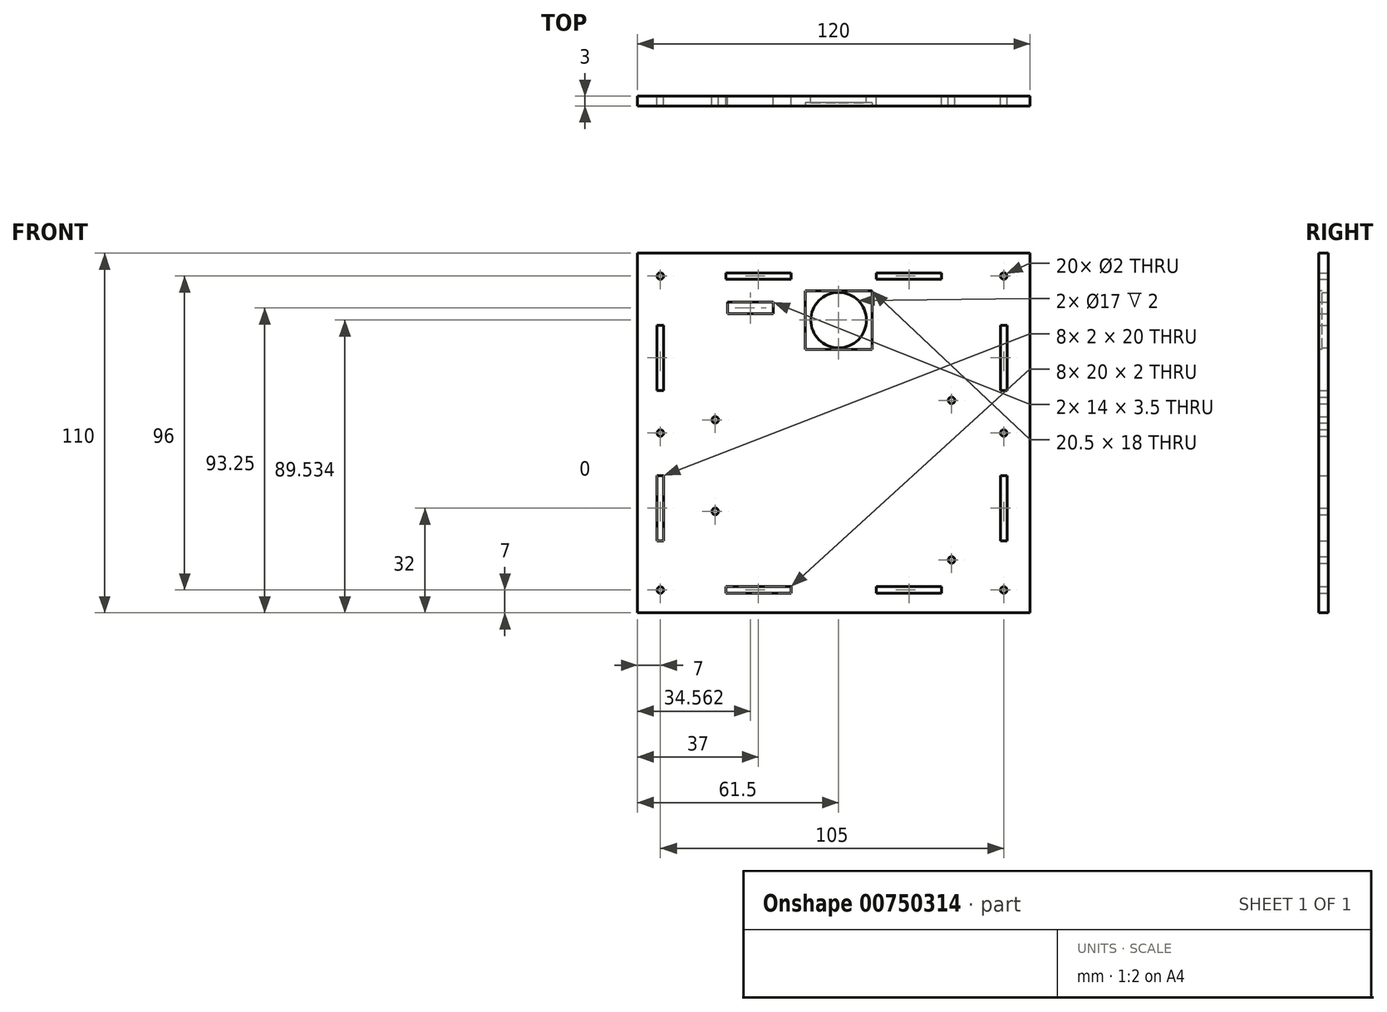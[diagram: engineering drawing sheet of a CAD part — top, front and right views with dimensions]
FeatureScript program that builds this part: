
annotation { "Feature Type Name" : "Feature", "Feature Type Description" : "" }
export const myFeature = defineFeature(function(context is Context, id is Id, definition is map)
    precondition{}
    {
        {
            var Q0;
            Q0=qCreatedBy(makeId("Front.planeOp"),FACE);
            var sketch = newSketch(context, id + "F0", { "sketchPlane" : qUnion([Q0])});
            skLineSegment(sketch, "E0.bottom", {"start": v(60, -55) * mm, "end": v(-60, -55) * mm});
            skLineSegment(sketch, "E0.top", {"start": v(60, 55) * mm, "end": v(-60, 55) * mm});
            skLineSegment(sketch, "E0.left", {"start": v(60, -55) * mm, "end": v(60, 55) * mm});
            skLineSegment(sketch, "E0.right", {"start": v(-60, -55) * mm, "end": v(-60, 55) * mm});
            skPoint(sketch, "E0.middle", {"position": v(0, 0) * mm});
            skCircle(sketch, "E1", {"center": v(1.5, 34.53) * mm, "radius": 8.5 * mm});
            skLineSegment(sketch, "E2.bottom", {"start": v(-18.44, 36.5) * mm, "end": v(-32.44, 36.5) * mm});
            skLineSegment(sketch, "E2.top", {"start": v(-18.44, 40) * mm, "end": v(-32.44, 40) * mm});
            skLineSegment(sketch, "E2.left", {"start": v(-18.44, 36.5) * mm, "end": v(-18.44, 40) * mm});
            skLineSegment(sketch, "E2.right", {"start": v(-32.44, 36.5) * mm, "end": v(-32.44, 40) * mm});
            skPoint(sketch, "E2.middle", {"position": v(-25.44, 38.25) * mm});
            skCircle(sketch, "E3", {"center": v(36.03, 10) * mm, "radius": 1 * mm});
            skCircle(sketch, "E4", {"center": v(36.03, -38.8) * mm, "radius": 1 * mm});
            skCircle(sketch, "E5", {"center": v(-36.22, 4.04) * mm, "radius": 1 * mm});
            skCircle(sketch, "E6", {"center": v(-36.22, -23.96) * mm, "radius": 1 * mm});
            skCircle(sketch, "E7", {"center": v(-53, 48) * mm, "radius": 1 * mm});
            skCircle(sketch, "E8", {"center": v(-53, -48) * mm, "radius": 1 * mm});
            skCircle(sketch, "E9", {"center": v(52, -48) * mm, "radius": 1 * mm});
            skCircle(sketch, "E10", {"center": v(52, 48) * mm, "radius": 1 * mm});
            skCircle(sketch, "E11", {"center": v(-53, 0) * mm, "radius": 1 * mm});
            skCircle(sketch, "E12", {"center": v(52, 0) * mm, "radius": 1 * mm});
            skLineSegment(sketch, "E13.bottom", {"start": v(-52, 33) * mm, "end": v(-54, 33) * mm});
            skLineSegment(sketch, "E13.top", {"start": v(-52, 13) * mm, "end": v(-54, 13) * mm});
            skLineSegment(sketch, "E13.left", {"start": v(-52, 33) * mm, "end": v(-52, 13) * mm});
            skLineSegment(sketch, "E13.right", {"start": v(-54, 33) * mm, "end": v(-54, 13) * mm});
            skPoint(sketch, "E13.middle", {"position": v(-53, 23) * mm});
            skLineSegment(sketch, "E14.bottom", {"start": v(-52, -33) * mm, "end": v(-54, -33) * mm});
            skLineSegment(sketch, "E14.top", {"start": v(-52, -13) * mm, "end": v(-54, -13) * mm});
            skLineSegment(sketch, "E14.left", {"start": v(-52, -33) * mm, "end": v(-52, -13) * mm});
            skLineSegment(sketch, "E14.right", {"start": v(-54, -33) * mm, "end": v(-54, -13) * mm});
            skPoint(sketch, "E14.middle", {"position": v(-53, -23) * mm});
            skPoint(sketch, "E14.cornerSnap0", {"position": v(-52, 23) * mm});
            skLineSegment(sketch, "E15.bottom", {"start": v(53, 13) * mm, "end": v(51, 13) * mm});
            skLineSegment(sketch, "E15.top", {"start": v(53, 33) * mm, "end": v(51, 33) * mm});
            skLineSegment(sketch, "E15.left", {"start": v(53, 13) * mm, "end": v(53, 33) * mm});
            skLineSegment(sketch, "E15.right", {"start": v(51, 13) * mm, "end": v(51, 33) * mm});
            skPoint(sketch, "E15.middle", {"position": v(52, 23) * mm});
            skLineSegment(sketch, "E16.bottom", {"start": v(53, -33) * mm, "end": v(51, -33) * mm});
            skLineSegment(sketch, "E16.top", {"start": v(53, -13) * mm, "end": v(51, -13) * mm});
            skLineSegment(sketch, "E16.left", {"start": v(53, -33) * mm, "end": v(53, -13) * mm});
            skLineSegment(sketch, "E16.right", {"start": v(51, -33) * mm, "end": v(51, -13) * mm});
            skPoint(sketch, "E16.middle", {"position": v(52, -23) * mm});
            skLineSegment(sketch, "E17.bottom", {"start": v(-13, -49) * mm, "end": v(-33, -49) * mm});
            skLineSegment(sketch, "E17.top", {"start": v(-13, -47) * mm, "end": v(-33, -47) * mm});
            skLineSegment(sketch, "E17.left", {"start": v(-13, -49) * mm, "end": v(-13, -47) * mm});
            skLineSegment(sketch, "E17.right", {"start": v(-33, -49) * mm, "end": v(-33, -47) * mm});
            skPoint(sketch, "E17.middle", {"position": v(-23, -48) * mm});
            skLineSegment(sketch, "E18.bottom", {"start": v(33, -49) * mm, "end": v(13, -49) * mm});
            skLineSegment(sketch, "E18.top", {"start": v(33, -47) * mm, "end": v(13, -47) * mm});
            skLineSegment(sketch, "E18.left", {"start": v(33, -49) * mm, "end": v(33, -47) * mm});
            skLineSegment(sketch, "E18.right", {"start": v(13, -49) * mm, "end": v(13, -47) * mm});
            skPoint(sketch, "E18.middle", {"position": v(23, -48) * mm});
            skLineSegment(sketch, "E19.bottom", {"start": v(-13, 47) * mm, "end": v(-33, 47) * mm});
            skLineSegment(sketch, "E19.top", {"start": v(-13, 49) * mm, "end": v(-33, 49) * mm});
            skLineSegment(sketch, "E19.left", {"start": v(-13, 47) * mm, "end": v(-13, 49) * mm});
            skLineSegment(sketch, "E19.right", {"start": v(-33, 47) * mm, "end": v(-33, 49) * mm});
            skPoint(sketch, "E19.middle", {"position": v(-23, 48) * mm});
            skLineSegment(sketch, "E20.bottom", {"start": v(33, 47) * mm, "end": v(13, 47) * mm});
            skLineSegment(sketch, "E20.top", {"start": v(33, 49) * mm, "end": v(13, 49) * mm});
            skLineSegment(sketch, "E20.left", {"start": v(33, 47) * mm, "end": v(33, 49) * mm});
            skLineSegment(sketch, "E20.right", {"start": v(13, 47) * mm, "end": v(13, 49) * mm});
            skPoint(sketch, "E20.middle", {"position": v(23, 48) * mm});
            skSolve(sketch);
        }
        {
            var Q0;
            Q0=makeQuery(id+"F0.imprint","IMPRINT",FACE,{"disambiguationData":[TD([[makeQuery(id+"F0.imprint","IMPRINT",EDGE,{"derivedFrom":sQuery(id+"F0.wireOp",EDGE,"E0.bottom")}),-1.0]])]});
            extrude(context, id + "F1", {"entities" : qUnion([Q0]), "depth" : 3 * mm, "offsetDistance" : 25 * mm});
        }
        {
            var Q0;
            Q0=makeQuery(id+"F1.opExtrude","CAP_FACE",FACE,{"disambiguationData":[OSD([sQuery(id+"F0.wireOp",EDGE,"E0.bottom"),sQuery(id+"F0.wireOp",EDGE,"E0.top"),sQuery(id+"F0.wireOp",EDGE,"E0.left"),sQuery(id+"F0.wireOp",EDGE,"E0.right"),sQuery(id+"F0.wireOp",EDGE,"E1"),sQuery(id+"F0.wireOp",EDGE,"E2.bottom"),sQuery(id+"F0.wireOp",EDGE,"E2.top"),sQuery(id+"F0.wireOp",EDGE,"E2.left"),sQuery(id+"F0.wireOp",EDGE,"E2.right"),sQuery(id+"F0.wireOp",EDGE,"E3"),sQuery(id+"F0.wireOp",EDGE,"E4"),sQuery(id+"F0.wireOp",EDGE,"E5"),sQuery(id+"F0.wireOp",EDGE,"E6"),sQuery(id+"F0.wireOp",EDGE,"E7"),sQuery(id+"F0.wireOp",EDGE,"E8"),sQuery(id+"F0.wireOp",EDGE,"E9"),sQuery(id+"F0.wireOp",EDGE,"E10"),sQuery(id+"F0.wireOp",EDGE,"E11"),sQuery(id+"F0.wireOp",EDGE,"E12"),sQuery(id+"F0.wireOp",EDGE,"E13.bottom"),sQuery(id+"F0.wireOp",EDGE,"E13.top"),sQuery(id+"F0.wireOp",EDGE,"E13.left"),sQuery(id+"F0.wireOp",EDGE,"E13.right"),sQuery(id+"F0.wireOp",EDGE,"E14.bottom"),sQuery(id+"F0.wireOp",EDGE,"E14.top"),sQuery(id+"F0.wireOp",EDGE,"E14.left"),sQuery(id+"F0.wireOp",EDGE,"E14.right"),sQuery(id+"F0.wireOp",EDGE,"E15.bottom"),sQuery(id+"F0.wireOp",EDGE,"E15.top"),sQuery(id+"F0.wireOp",EDGE,"E15.left"),sQuery(id+"F0.wireOp",EDGE,"E15.right"),sQuery(id+"F0.wireOp",EDGE,"E16.bottom"),sQuery(id+"F0.wireOp",EDGE,"E16.top"),sQuery(id+"F0.wireOp",EDGE,"E16.left"),sQuery(id+"F0.wireOp",EDGE,"E16.right"),sQuery(id+"F0.wireOp",EDGE,"E17.bottom"),sQuery(id+"F0.wireOp",EDGE,"E17.top"),sQuery(id+"F0.wireOp",EDGE,"E17.left"),sQuery(id+"F0.wireOp",EDGE,"E17.right"),sQuery(id+"F0.wireOp",EDGE,"E18.bottom"),sQuery(id+"F0.wireOp",EDGE,"E18.top"),sQuery(id+"F0.wireOp",EDGE,"E18.left"),sQuery(id+"F0.wireOp",EDGE,"E18.right"),sQuery(id+"F0.wireOp",EDGE,"E19.bottom"),sQuery(id+"F0.wireOp",EDGE,"E19.top"),sQuery(id+"F0.wireOp",EDGE,"E19.left"),sQuery(id+"F0.wireOp",EDGE,"E19.right"),sQuery(id+"F0.wireOp",EDGE,"E20.bottom"),sQuery(id+"F0.wireOp",EDGE,"E20.top"),sQuery(id+"F0.wireOp",EDGE,"E20.left"),sQuery(id+"F0.wireOp",EDGE,"E20.right")])],"isStart":false});
            var sketch = newSketch(context, id + "F2", { "sketchPlane" : qUnion([Q0])});
            skLineSegment(sketch, "E21.bottom", {"start": v(11.75, 25.53) * mm, "end": v(-8.75, 25.53) * mm});
            skLineSegment(sketch, "E21.top", {"start": v(11.75, 43.53) * mm, "end": v(-8.75, 43.53) * mm});
            skLineSegment(sketch, "E21.left", {"start": v(11.75, 25.53) * mm, "end": v(11.75, 43.53) * mm});
            skLineSegment(sketch, "E21.right", {"start": v(-8.75, 25.53) * mm, "end": v(-8.75, 43.53) * mm});
            skPoint(sketch, "E21.middle", {"position": v(1.5, 34.53) * mm});
            skSolve(sketch);
        }
        {
            var Q0;
            Q0=makeQuery(id+"F2.imprint","IMPRINT",FACE,{"disambiguationData":[TD([[makeQuery(id+"F2.imprint","IMPRINT",EDGE,{"derivedFrom":sQuery(id+"F2.wireOp",EDGE,"E21.bottom")}),-1.0]])]});
            extrude(context, id + "F3", {"entities" : qUnion([Q0]), "operationType" : NewBodyOperationType.REMOVE, "oppositeDirection" : true, "depth" : 1 * mm, "offsetDistance" : 25 * mm});
        }
    });
